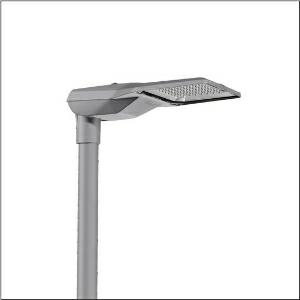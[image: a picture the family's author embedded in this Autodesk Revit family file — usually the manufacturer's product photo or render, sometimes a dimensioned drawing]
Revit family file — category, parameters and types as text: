
# Revit family: streetlight_sl_21_midi___st0_5a_5xe3b43s08mb_23ad
name_source: partatom
category: Lighting Fixtures
units: mm (PartAtom-declared; Revit-internal decimal feet)

## family parameters
Cut with Voids When Loaded = No
Host = Face
Light Source = No
Part Type = Normal
Room Calculation Point = No
Round Connector Dimension = Use Diameter
Shared = No

## types (1)
- --- (1 x LED, 20180 lm, 147 W, 4000K)
    Apparent Load = 147 VA
    CIE Flux Codes = 41 75 97 100 100
    Color Rendering = 70
    Color Temperature = 4000K
    Default Elevation = 1800 mm
    Description = Streetlight SL 21 midi, mast luminaire, primary light control with lens, of PMMA, primary optical cover: cover, of toughened safety glass, transparent, light distribution: ST0.5a, light emission: direct distribution, primary light characteristic: asymmetric, installation type: side-entry, post-top, LED, High Power LED, rated luminous flux: 20.180lm, luminous efficacy: 137lm/W, light colour: 740, colour temperature: 4000K, control gear: D4i, control: overheat protection, constant luminous flux control, time-dependent luminous flux control, flexible luminous flux parameterisation, pre-setting: logarithmic dimming characteristic, mains connection: 230..240V, AC, 50/60Hz, start of lifetime: 147W, end of service life: 155W, reduction: 65W, luminaire housing, of diecast aluminium, powder-coated, Siteco® metallic grey (DB 702S), corrosivity category C5 mid according to DIN EN ISO 12944, please order mast flange separately, inclination adjustable: 0°, 5°, 10°, 15°, sealing non-destructively replaceable, multi-level sealing system, length: 644mm, width: 335mm, height: 110mm, mast flange for spigot size: 42mm (side-entry): 5XC10008XM4, 60/48mm (side-entry/post-top): 5XC10108XM2, 76/60mm (side-entry/post-top): 5XC10108XM1, mounting height: 4..8m, Smart Interface above, protection rating (complete): IP66, insulation class (complete): insulation class II (safety insulation), certification: CE, ENEC, ENEC+, VDE, impact resistance: IK10, permissible operating ambient temperature for outdoor applications: -40..+50°C, standard-compliant lighting for roads and squares, packaging unit: 1 piece

Light Distribution: ST0.5a
    Height = 111 mm
    Lamp = 1 x LED
    Lamp Light Flux = 20180 lm
    Lamp Power = 147 W
    Lamp count = 1
    Length = 644 mm
    Luminous efficacy = 137 lm/W
    Manufacturer = Siteco
    ModVariant = No
    Model = 5XE3B43S08MB
    Number of Poles = 1
    OnlyDefault = Yes
    Power Factor = 1
    Product Name = Streetlight SL 21 midi | ST0.5a
    Product group = mast luminaire | pylon top
    ProductGroupID = 6100
    Protection Class = Protection class II
    Protection Degree = IP 66
    RLX_Detail_Level = 1
    RLX_Emergency_Light_Flux = 0 lm
    RLX_Emergency_Type = 0
    RLX_Emergency_Type_DB = No
    RlxData = <blob elided: 37889 chars, md5=187b7394>
    Socket = socket
    Standby Power = 0 W
    System Light Flux = 20180 lm
    System Power = 147 W
    Type Comments = factory setting: luminous flux: 100 % | dim-lin: 254 | 750 mA
    Type Image = l_1004302.jpg
    URL = http://relux.com
    VarID = @adj_212983
    Voltage = 0 V
    Weight = 0.00 kg
    Width = 336 mm

## geometry (parser evidence)
native form markers: Blend x4, Sweep x9
no freeform markers — native parametric forms only
